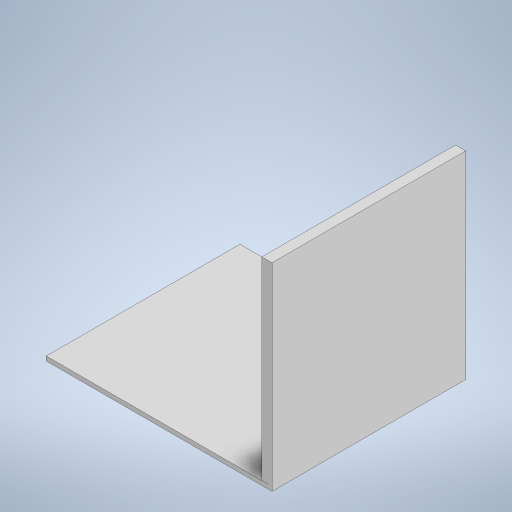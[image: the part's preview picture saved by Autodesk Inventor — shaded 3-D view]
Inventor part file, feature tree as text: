
AUTODESK INVENTOR PART (.ipt)
format: ipt  version: 2024 (Build 280153000, 153)  size: 322,560 bytes
history: native  units: mm
features: extrude x11, sketch x11
ambient origin geometry x8: Origin, YZ Plane, XZ Plane, XY Plane, X Axis, Y Axis, Z Axis, Center Point
bodies: Solid1 (feature_tree)
feature tree (22):
  extrude  "Top"  Depth=160.0mm
  extrude  "Right"  Depth=179.5mm
  extrude  "Left"  Depth=215.9mm
  extrude  "Plexiglass Cut"  Depth=25.4mm
  extrude  "Bottom"  Depth=266.7mm TaperAngle=0.0deg
  extrude  "Top Flattening"  Depth=266.7mm TaperAngle=0.0deg
  extrude  "Outer Side Flattening"  Depth=12.7mm TaperAngle=0.0deg
  extrude  "Bottom Flattening"  Depth=22.4mm TaperAngle=0.0deg
  extrude  "Inner Flattening"  Depth=22.389425mm
  extrude  "Top Cut"  Depth=22.4mm TaperAngle=0.0deg
  extrude  "Quarter Cut"  Depth=22.4mm TaperAngle=0.0deg
  sketch  "Sketch1"  dims[d11=220.0mm d12=160.0mm]
  sketch  "Sketch3"  dims[d15=248.6mm d16=179.5mm]
  sketch  "Sketch4"  dims[d18=304.8mm d19=215.9mm]
  sketch  "Sketch5"  dims[d20=25.4mm d21=0.0mm d22=25.4mm]
  sketch  "Sketch6"  dims[d25=266.7mm d26=50.8mm d27=0.0mm]
  sketch  "Sketch9"  dims[d28=266.7mm d29=50.8mm d30=0.0mm]
  sketch  "Sketch10"  dims[d31=12.7mm d32=304.8mm d33=0.0mm]
  sketch  "Sketch11"  dims[d34=25.4mm d35=0.0mm d46=22.4mm d47=0.0mm]
  sketch  "Sketch12"  dims[d48=22.389425mm d49=22.389425mm]
  sketch  "Sketch13"  dims[d50=0.0mm d51=0.0mm d52=22.4mm d53=0.0mm]
  sketch  "Sketch14"  dims[d54=296.8mm d55=22.4mm d56=0.0mm d57=0.0mm d58=0.0mm d59=0.0mm d60=0.0mm]
